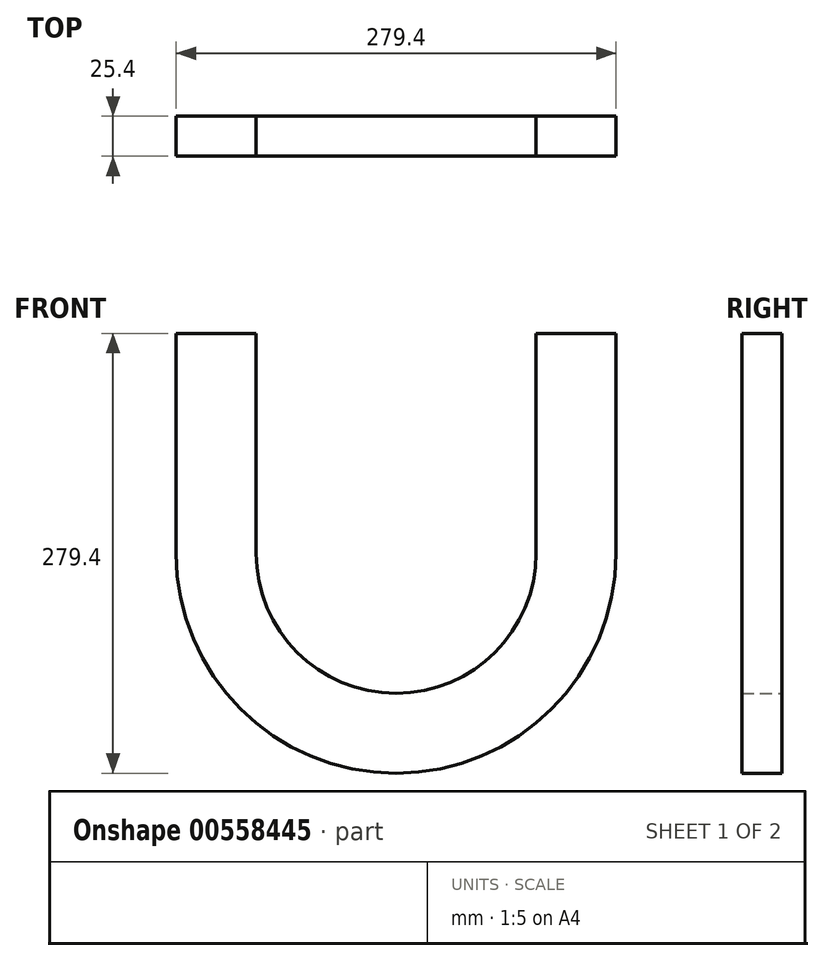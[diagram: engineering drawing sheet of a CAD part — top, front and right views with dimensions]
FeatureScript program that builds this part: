
annotation { "Feature Type Name" : "Feature", "Feature Type Description" : "" }
export const myFeature = defineFeature(function(context is Context, id is Id, definition is map)
    precondition{}
    {
        {
            var Q0;
            Q0=qCreatedBy(makeId("Front.planeOp"),FACE);
            var sketch = newSketch(context, id + "F0", { "sketchPlane" : qUnion([Q0])});
            skArc(sketch, "E0", {"start": v(-139.7, 0) * mm, "mid": v(0, -139.7) * mm, "end": v(139.7, 0) * mm});
            skArc(sketch, "E1", {"start": v(-88.9, 0) * mm, "mid": v(0, -88.9) * mm, "end": v(88.9, 0) * mm});
            skLineSegment(sketch, "E2", {"start": v(-139.7, 0) * mm, "end": v(-139.7, 139.7) * mm});
            skLineSegment(sketch, "E3", {"start": v(-139.7, 139.7) * mm, "end": v(-88.9, 139.7) * mm});
            skLineSegment(sketch, "E4", {"start": v(-88.9, 139.7) * mm, "end": v(-88.9, 0) * mm});
            skLineSegment(sketch, "E5", {"start": v(139.7, 0) * mm, "end": v(139.7, 139.7) * mm});
            skLineSegment(sketch, "E6", {"start": v(139.7, 139.7) * mm, "end": v(88.9, 139.7) * mm});
            skLineSegment(sketch, "E7", {"start": v(88.9, 139.7) * mm, "end": v(88.9, 0) * mm});
            skSolve(sketch);
        }
        {
            var Q0;
            Q0 = qSketchRegion(id + "F0", true);
            extrude(context, id + "F1", {"entities" : qUnion([Q0]), "depth" : 25.4 * mm, "offsetDistance" : 25.4 * mm});
        }
    });
